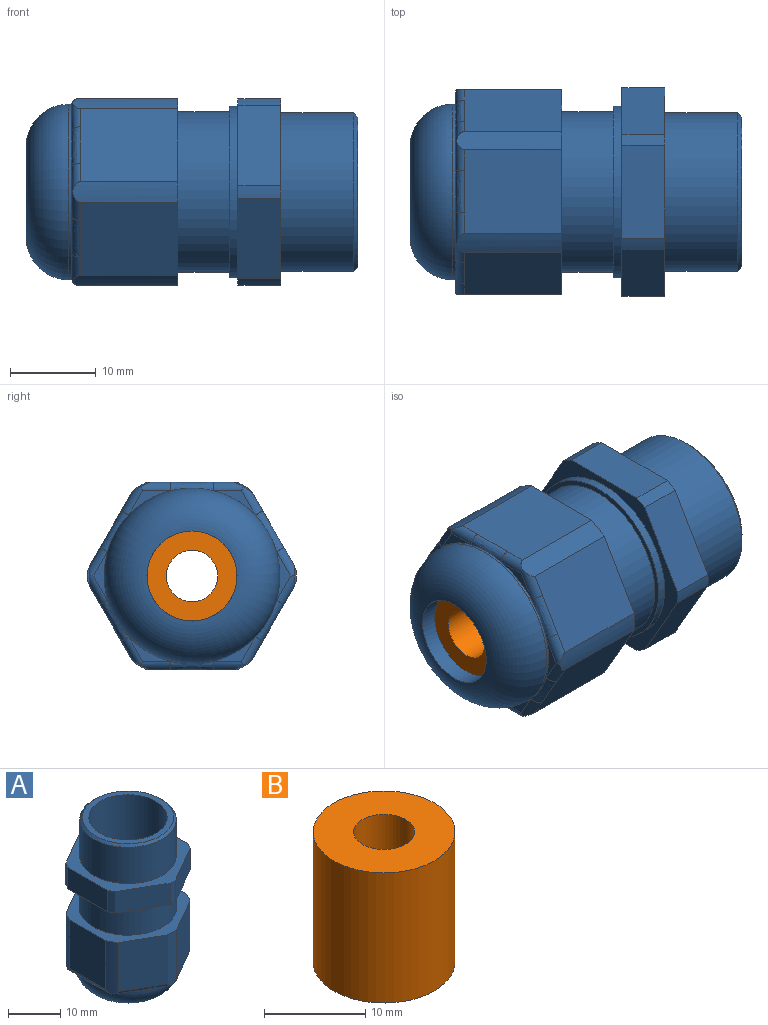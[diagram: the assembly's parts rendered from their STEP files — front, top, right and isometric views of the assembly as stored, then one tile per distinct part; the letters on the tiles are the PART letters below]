
ASSEMBLY  parts=2 mates=1
PART A: 109 faces, bbox 22.2x25x38.7 mm
  f0: torus R=5.25mm, axis (0,0,1), area 416.2mm2, adj f2,f7
  f1: cylinder r=7.5mm len=15mm, axis (0,0,1), area 565.5mm2, adj f43,f45
  f2: cylinder r=5.25mm len=10.5mm, axis (0,0,-1), area 66mm2, adj f0,f44
  f3: cone r=8.75mm half-angle=45deg, axis (0,0,-1), area 40mm2, adj f4,f43
  f4: cylinder r=9.25mm len=18.5mm, axis (0,0,-1), area 494mm2, adj f3,f15
  f5: cylinder r=10mm len=20mm, axis (0,0,-1), area 62.8mm2, adj f16,f36
  f6: cylinder r=9.38mm len=18.75mm, axis (0,0,-1), area 353.4mm2, adj f22,f36
  f7: cylinder r=10.25mm len=20.5mm, axis (0,0,-1), area 19.3mm2, adj f0,f10,f11,f12,f13,f14,f23,f47
  f8: cylinder r=7.4mm len=24.7mm, axis (0,0,-1), area 1148.4mm2, adj f44,f45
  f9: plane 9.38x5.42mm, normal (0.5,0.87,0), area 48.4mm2, adj f15,f16,f41,f42,f64,f65,f66,f67
  f10: plane 4.92x2.84mm, normal (0,0,-1), area 3.1mm2, adj f7,f58,f60
  f11: plane 4.92x2.84mm, normal (0,0,-1), area 3.1mm2, adj f7,f52,f54
  f12: plane 5.69x1.64mm, normal (0,0,-1), area 3.1mm2, adj f7,f46,f48
  f13: plane 4.92x2.84mm, normal (0,0,-1), area 3.1mm2, adj f7,f49,f51
  f14: plane 5.69x1.64mm, normal (0,0,-1), area 3.1mm2, adj f7,f61,f63
  f15: plane 24.3x21.75mm, normal (0,0,1), area 139.1mm2, adj f4,f9,f17,f18,f19,f20,f21,f37
  f16: plane 24.3x21.75mm, normal (0,0,-1), area 93.7mm2, adj f5,f9,f17,f18,f19,f20,f21,f37
  f17: plane 9.38x5.42mm, normal (-0.5,0.87,0), area 54.2mm2, adj f15,f16,f40,f41
  f18: plane 10.84x5mm, normal (-1,0,0), area 54.2mm2, adj f15,f16,f39,f40
  f19: plane 9.38x5.42mm, normal (-0.5,-0.87,0), area 54.2mm2, adj f15,f16,f38,f39
  f20: plane 9.38x5.42mm, normal (0.5,-0.87,0), area 54.2mm2, adj f15,f16,f37,f38
  f21: plane 10.84x5mm, normal (1,0,0), area 54.2mm2, adj f15,f16,f37,f42
  f22: plane 24x21.9mm, normal (0,0,1), area 134.7mm2, adj f6,f24,f25,f26,f27,f28,f29,f30
  f23: plane 4.92x2.84mm, normal (0,0,-1), area 3.1mm2, adj f7,f55,f57
  f24: plane 11.45x8.5mm, normal (0.5,0.87,0), area 112mm2, adj f22,f34,f35,f48,f50,f52
  f25: plane 11.45x8.5mm, normal (-0.5,0.87,0), area 112mm2, adj f22,f33,f34,f46,f47,f49
  f26: plane 11.45x9.82mm, normal (-1,0,0), area 112mm2, adj f22,f32,f33,f51,f53,f55
  f27: plane 11.45x8.5mm, normal (-0.5,-0.87,0), area 112mm2, adj f22,f31,f32,f57,f59,f61
  f28: plane 11.45x8.5mm, normal (0.5,-0.87,0), area 112mm2, adj f22,f30,f31,f60,f62,f63
  f29: plane 11.45x9.82mm, normal (1,0,0), area 112mm2, adj f22,f30,f35,f54,f56,f58
  f30: cylinder r=12mm len=12.3mm, axis (0,0,1), area 29mm2, adj f22,f28,f29,f58,f60
  f31: cylinder r=12mm len=12.3mm, axis (0,0,1), area 29mm2, adj f22,f27,f28,f61,f63
  f32: cylinder r=12mm len=12.3mm, axis (0,0,1), area 29mm2, adj f22,f26,f27,f55,f57
  f33: cylinder r=12mm len=12.3mm, axis (0,0,1), area 29mm2, adj f22,f25,f26,f49,f51
  f34: cylinder r=12mm len=12.3mm, axis (0,0,1), area 29mm2, adj f22,f24,f25,f46,f48
  f35: cylinder r=12mm len=12.3mm, axis (0,0,1), area 29mm2, adj f22,f24,f29,f52,f54
  f36: plane 20x20mm, normal (0,0,-1), area 38mm2, adj f5,f6
  f37: cylinder r=12.15mm len=5mm, axis (0,0,1), area 7.5mm2, adj f15,f16,f20,f21
  f38: cylinder r=12.15mm len=5mm, axis (0,0,1), area 7.5mm2, adj f15,f16,f19,f20
  f39: cylinder r=12.15mm len=5mm, axis (0,0,1), area 7.5mm2, adj f15,f16,f18,f19
  f40: cylinder r=12.15mm len=5mm, axis (0,0,1), area 7.5mm2, adj f15,f16,f17,f18
  f41: cylinder r=12.15mm len=5mm, axis (0,0,1), area 7.5mm2, adj f9,f15,f16,f17
  f42: cylinder r=12.15mm len=5mm, axis (0,0,1), area 7.5mm2, adj f9,f15,f16,f21
  f43: plane 17.5x17.5mm, normal (0,0,1), area 63.8mm2, adj f1,f3
  f44: plane 14.8x14.8mm, normal (0,0,1), area 85.4mm2, adj f2,f8
  f45: plane 15x15mm, normal (0,0,1), area 4.7mm2, adj f1,f8
  f46: cylinder r=1mm len=3.56mm, axis (-0.87,-0.5,0), area 4.9mm2, adj f12,f25,f34,f47,f48
  f47: bspline ~4.76x3.33mm, area 6.7mm2, adj f7,f25,f46,f49
  f48: cylinder r=1mm len=3.56mm, axis (-0.87,0.5,0), area 4.9mm2, adj f12,f24,f34,f46,f50
  f49: cylinder r=1mm len=3.56mm, axis (-0.87,-0.5,0), area 4.9mm2, adj f13,f25,f33,f47,f51
  f50: bspline ~4.76x3.33mm, area 6.7mm2, adj f7,f24,f48,f52
  f51: cylinder r=1mm len=3.54mm, axis (0,-1,0), area 4.9mm2, adj f13,f26,f33,f49,f53
  f52: cylinder r=1mm len=3.56mm, axis (-0.87,0.5,0), area 4.9mm2, adj f11,f24,f35,f50,f54
  f53: bspline ~4.92x1mm, area 6.7mm2, adj f7,f26,f51,f55
  f54: cylinder r=1mm len=3.54mm, axis (0,1,0), area 4.9mm2, adj f11,f29,f35,f52,f56
  f55: cylinder r=1mm len=3.54mm, axis (0,-1,0), area 4.9mm2, adj f23,f26,f32,f53,f57
  f56: bspline ~4.92x1mm, area 6.7mm2, adj f7,f29,f54,f58
  f57: cylinder r=1mm len=3.56mm, axis (0.87,-0.5,0), area 4.9mm2, adj f23,f27,f32,f55,f59
  f58: cylinder r=1mm len=3.54mm, axis (0,1,0), area 4.9mm2, adj f10,f29,f30,f56,f60
  f59: bspline ~4.76x3.33mm, area 6.7mm2, adj f7,f27,f57,f61
  f60: cylinder r=1mm len=3.56mm, axis (0.87,0.5,0), area 4.9mm2, adj f10,f28,f30,f58,f62
  f61: cylinder r=1mm len=3.56mm, axis (0.87,-0.5,0), area 4.9mm2, adj f14,f27,f31,f59,f63
  f62: bspline ~4.76x3.33mm, area 6.7mm2, adj f7,f28,f60,f63
  f63: cylinder r=1mm len=3.56mm, axis (0.87,0.5,0), area 4.9mm2, adj f14,f28,f31,f61,f62
  f64: plane 2.12x0.09mm, normal (0.87,-0.5,0), area 0.2mm2, adj f9,f65,f70,f71
  f65: plane 0.42x0.3mm, normal (0,0,1), area 0mm2, adj f9,f64,f66,f71
  f66: extruded ~0.76x0.6mm, area 0.1mm2, adj f9,f65,f67,f71
  f67: extruded ~0.56x0.43mm, area 0.1mm2, adj f9,f66,f68,f71
  f68: extruded ~0.42x0.3mm, area 0mm2, adj f9,f67,f69,f71
  f69: plane 0.92x0.09mm, normal (-0.87,0.5,0), area 0.1mm2, adj f9,f68,f70,f71
  f70: plane 0.38x0.28mm, normal (0,0,-1), area 0mm2, adj f9,f64,f69,f71
  f71: plane 2.12x1.08mm, normal (0.5,0.87,0), area 1.5mm2, adj f64,f65,f66,f67,f68,f69,f70,f72
  f72: plane 0.43x0.09mm, normal (-0.87,0.5,0), area 0mm2, adj f71,f73,f77,f78
  f73: plane 0.15x0.15mm, normal (0,0,-1), area 0mm2, adj f71,f72,f74,f78
  f74: extruded ~0.28x0.22mm, area 0mm2, adj f71,f73,f75,f78
  f75: extruded ~0.18x0.14mm, area 0mm2, adj f71,f74,f76,f78
  f76: extruded ~0.36x0.26mm, area 0mm2, adj f71,f75,f77,f78
  f77: plane 0.17x0.15mm, normal (0,0,1), area 0mm2, adj f71,f72,f76,f78
  f78: plane 0.43x0.42mm, normal (0.5,0.87,0), area 0.2mm2, adj f72,f73,f74,f75,f76,f77
  f79: plane 0.35x0.25mm, normal (0.73,-0.42,0.54), area 0mm2, adj f9,f80,f84,f85
  f80: plane 0.56x0.38mm, normal (0,0,1), area 0.1mm2, adj f9,f79,f81,f85
  f81: plane 2.12x0.09mm, normal (-0.87,0.5,0), area 0.2mm2, adj f9,f80,f82,f85
  f82: plane 0.38x0.28mm, normal (0,0,-1), area 0mm2, adj f9,f81,f83,f85
  f83: plane 1.76x0.09mm, normal (0.87,-0.5,0), area 0.2mm2, adj f9,f82,f84,f85
  f84: plane 0.43x0.3mm, normal (0,0,-1), area 0mm2, adj f9,f79,f83,f85
  f85: plane 2.12x0.71mm, normal (0.5,0.87,0), area 0.9mm2, adj f79,f80,f81,f82,f83,f84
  f86: plane 0.35x0.25mm, normal (0.73,-0.42,0.54), area 0mm2, adj f9,f87,f91,f92
  f87: plane 0.56x0.38mm, normal (0,0,1), area 0.1mm2, adj f9,f86,f88,f92
  f88: plane 2.12x0.09mm, normal (-0.87,0.5,0), area 0.2mm2, adj f9,f87,f89,f92
  f89: plane 0.38x0.28mm, normal (0,0,-1), area 0mm2, adj f9,f88,f90,f92
  f90: plane 1.76x0.09mm, normal (0.87,-0.5,0), area 0.2mm2, adj f9,f89,f91,f92
  f91: plane 0.43x0.3mm, normal (0,0,-1), area 0mm2, adj f9,f86,f90,f92
  f92: plane 2.12x0.71mm, normal (0.5,0.87,0), area 0.9mm2, adj f86,f87,f88,f89,f90,f91
  f93: extruded ~0.39x0.29mm, area 0mm2, adj f9,f94,f107,f108
  f94: plane 0.3x0.28mm, normal (-0.6,0.35,-0.72), area 0mm2, adj f9,f93,f95,f108
  f95: extruded ~0.6x0.41mm, area 0.1mm2, adj f9,f94,f96,f108
  f96: extruded ~0.72x0.7mm, area 0.1mm2, adj f9,f95,f97,f108
  f97: extruded ~0.74x0.72mm, area 0.1mm2, adj f9,f96,f98,f108
  f98: extruded ~0.56x0.38mm, area 0.1mm2, adj f9,f97,f99,f108
  f99: plane 0.58x0.39mm, normal (0,0,-1), area 0.1mm2, adj f9,f98,f100,f108
  f100: plane 0.38x0.09mm, normal (0.87,-0.5,0), area 0mm2, adj f9,f99,f101,f108
  f101: plane 0.96x0.61mm, normal (0,0,1), area 0.1mm2, adj f9,f100,f102,f108
  f102: plane 0.09x0.09mm, normal (-0.87,0.5,0.03), area 0mm2, adj f9,f101,f103,f108
  f103: extruded ~1.05x0.96mm, area 0.2mm2, adj f9,f102,f104,f108
  f104: extruded ~1.12x1.04mm, area 0.2mm2, adj f9,f103,f105,f108
  f105: cylinder r=1.07mm len=0.73mm, axis (-0.5,-0.87,0), area 0.1mm2, adj f9,f104,f106,f108
  f106: extruded ~0.79x0.52mm, area 0.1mm2, adj f9,f105,f107,f108
  f107: cylinder r=1.36mm len=0.5mm, axis (-0.5,-0.87,0), area 0.1mm2, adj f9,f93,f106,f108
  f108: plane 2.23x1.9mm, normal (0.5,0.87,0), area 2.3mm2, adj f93,f94,f95,f96,f97,f98,f99,f100
PART B: 4 faces, bbox 14x14x15.7 mm
  f0: plane 14x14mm, normal (0,0,1), area 125.7mm2, adj f2,f3
  f1: plane 14x14mm, normal (0,0,-1), area 125.7mm2, adj f2,f3
  f2: cylinder r=3mm len=15.7mm, axis (0,0,-1), area 295.9mm2, adj f0,f1
  f3: cylinder r=7mm len=15.7mm, axis (0,0,-1), area 690.5mm2, adj f0,f1
PLACE A rot(axis=(0,1,0),90deg) t=(-29.7,0,0)mm
PLACE B rot(axis=(-0.58,0.58,-0.58),120deg) t=(-29.7,0,0)mm
MATE fastened B.f3 <-> A.f0  axis (-1,0,0) through (-27.7,0,0)mm
